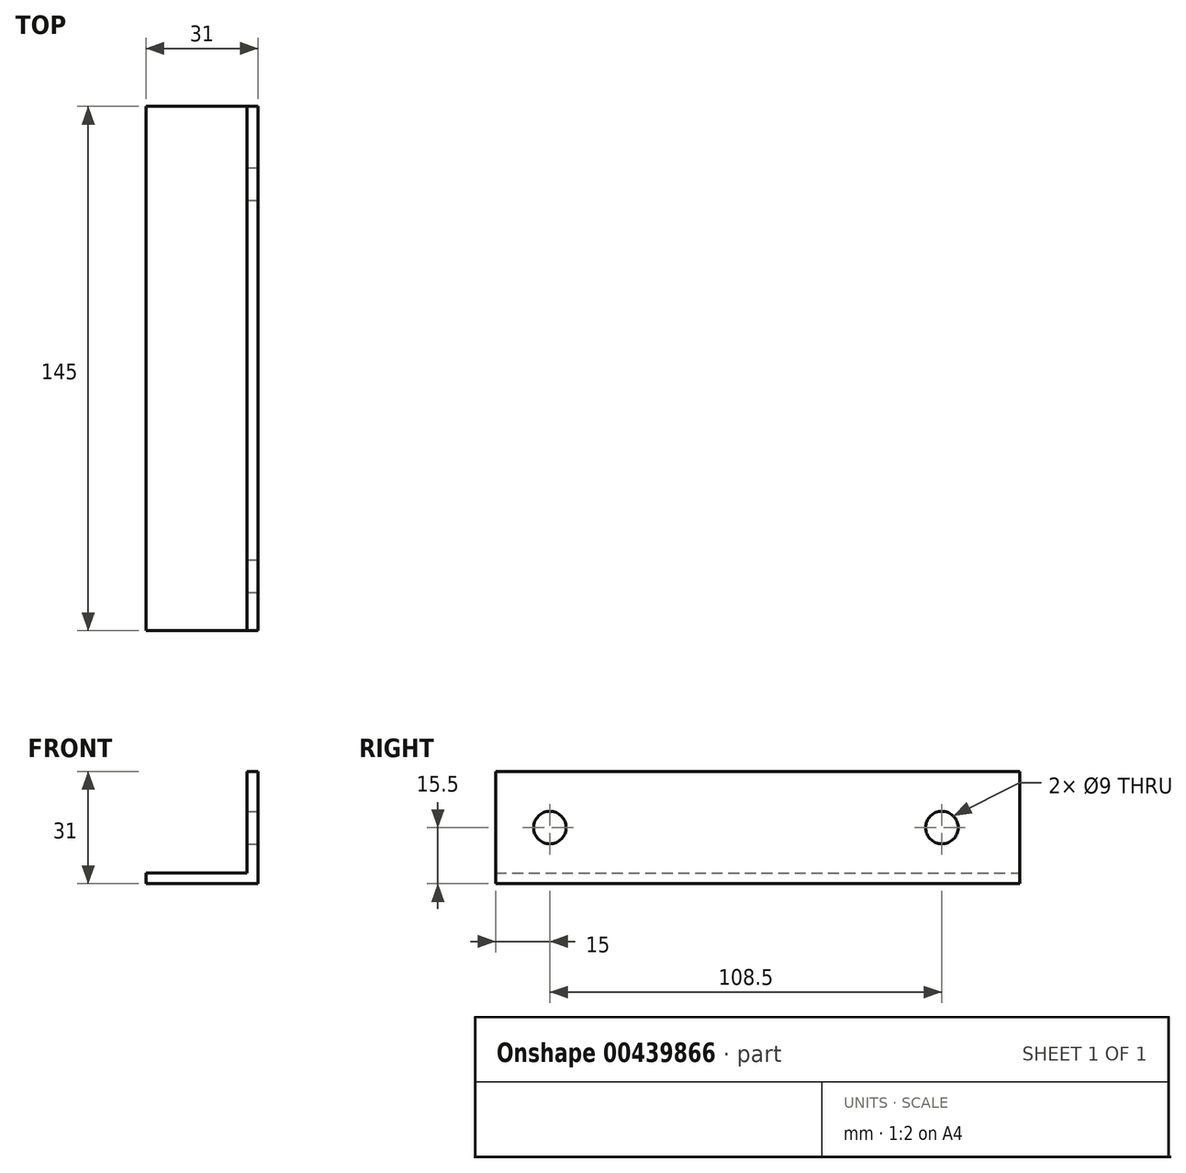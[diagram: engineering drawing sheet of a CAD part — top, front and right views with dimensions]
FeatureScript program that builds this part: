
annotation { "Feature Type Name" : "Feature", "Feature Type Description" : "" }
export const myFeature = defineFeature(function(context is Context, id is Id, definition is map)
    precondition{}
    {
        {
            assignVariable(context, id + "F0", {"name" : "x3", "anyValue" : 115});
        }
        {
            assignVariable(context, id + "F1", {"name" : "x4", "anyValue" : 15});
        }
        {
            assignVariable(context, id + "F2", {"name" : "x5", "anyValue" : 60});
        }
        {
            var Q0;
            Q0=qCreatedBy(makeId("Front.planeOp"),FACE);
            var sketch = newSketch(context, id + "F3", { "sketchPlane" : qUnion([Q0])});
            skLineSegment(sketch, "E0", {"start": v(0, 0) * mm, "end": v(0, 31) * mm});
            skLineSegment(sketch, "E1", {"start": v(0, 31) * mm, "end": v(-3, 31) * mm});
            skLineSegment(sketch, "E2", {"start": v(-3, 31) * mm, "end": v(-3, 3) * mm});
            skLineSegment(sketch, "E3", {"start": v(-3, 3) * mm, "end": v(-31, 3) * mm});
            skLineSegment(sketch, "E4", {"start": v(-31, 3) * mm, "end": v(-31, 0) * mm});
            skLineSegment(sketch, "E5", {"start": v(-31, 0) * mm, "end": v(0, 0) * mm});
            skSolve(sketch);
        }
        {
            var Q0;
            Q0=makeQuery(id+"F3.imprint","IMPRINT",FACE,{"disambiguationData":[TD([[makeQuery(id+"F3.imprint","IMPRINT",EDGE,{"derivedFrom":sQuery(id+"F3.wireOp",EDGE,"E0")}),1.0]])]});
            extrude(context, id + "F4", {"entities" : qUnion([Q0]), "depth" : (getVariable(context, 'x3') - getVariable(context, 'x4') + (0.75 * getVariable(context, 'x5'))) * mm});
        }
        {
            var Q0;
            Q0=makeQuery(id+"F4.opExtrude","SWEPT_FACE",FACE,{"disambiguationData":[OSD([sQuery(id+"F3.wireOp",EDGE,"E0")])]});
            var sketch = newSketch(context, id + "F5", { "sketchPlane" : qUnion([Q0])});
            skCircle(sketch, "E6", {"center": v(-21.5, 15.5) * mm, "radius": 4.5 * mm});
            skCircle(sketch, "E7", {"center": v(-130, 15.5) * mm, "radius": 4.5 * mm});
            skPoint(sketch, "E7.centerSnap0", {"position": v(-145, 15.5) * mm});
            skSolve(sketch);
        }
        {
            var Q0;
            Q0=makeQuery(id+"F5.imprint","IMPRINT",FACE,{"disambiguationData":[TD([[makeQuery(id+"F5.imprint","IMPRINT",EDGE,{"derivedFrom":sQuery(id+"F5.wireOp",EDGE,"E7")}),1.0]])]});
            var Q1;
            Q1=makeQuery(id+"F5.imprint","IMPRINT",FACE,{"disambiguationData":[TD([[makeQuery(id+"F5.imprint","IMPRINT",EDGE,{"derivedFrom":sQuery(id+"F5.wireOp",EDGE,"E6")}),1.0]])]});
            extrude(context, id + "F6", {"entities" : qUnion([Q0, Q1]), "operationType" : NewBodyOperationType.REMOVE, "endBound" : BoundingType.UP_TO_NEXT, "oppositeDirection" : true, "depth" : 25 * mm});
        }
    });
